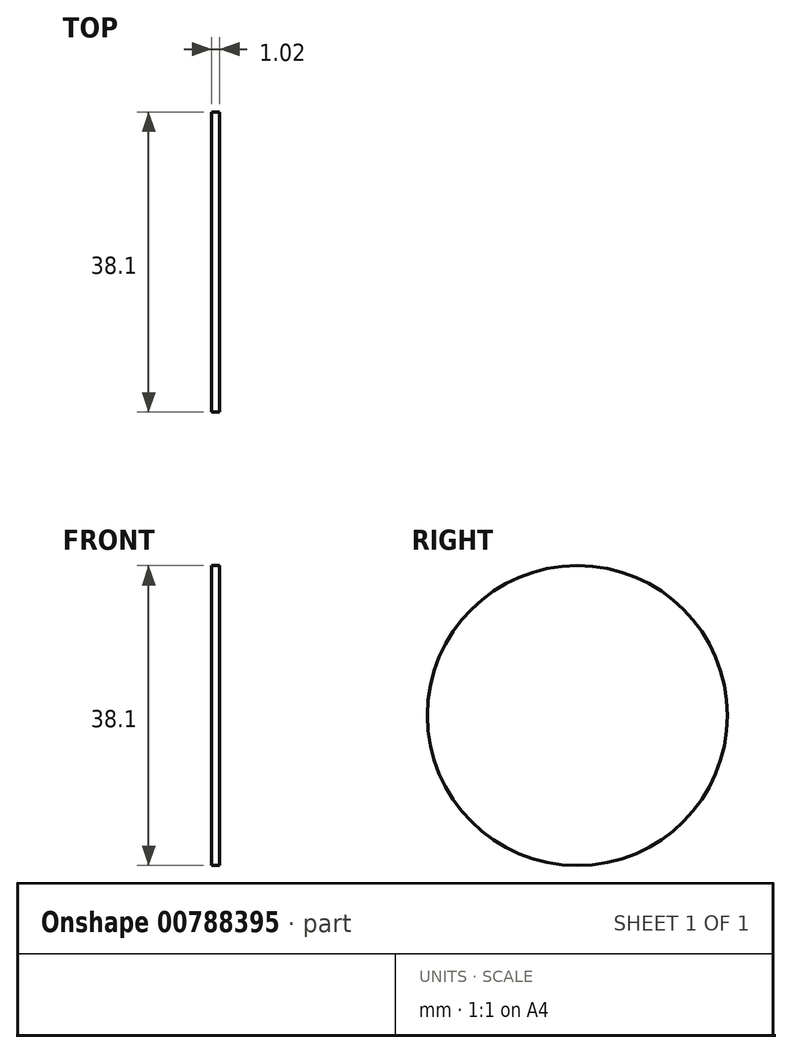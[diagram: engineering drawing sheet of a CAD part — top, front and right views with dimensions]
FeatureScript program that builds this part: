
annotation { "Feature Type Name" : "Feature", "Feature Type Description" : "" }
export const myFeature = defineFeature(function(context is Context, id is Id, definition is map)
    precondition{}
    {
        {
            var Q0;
            Q0=qCreatedBy(makeId("Right.planeOp"),FACE);
            var sketch = newSketch(context, id + "F0", { "sketchPlane" : qUnion([Q0])});
            skCircle(sketch, "E0", {"center": v(-17.14, 37.67) * mm, "radius": 19.05 * mm});
            skSolve(sketch);
        }
        {
            var Q0;
            Q0=makeQuery(id+"F0.imprint","IMPRINT",FACE,{"disambiguationData":[TD([[makeQuery(id+"F0.imprint","IMPRINT",EDGE,{"derivedFrom":sQuery(id+"F0.wireOp",EDGE,"E0")}),1.0]])]});
            extrude(context, id + "F1", {"entities" : qUnion([Q0]), "depth" : 1.02 * mm, "offsetDistance" : 25.4 * mm});
        }
    });
